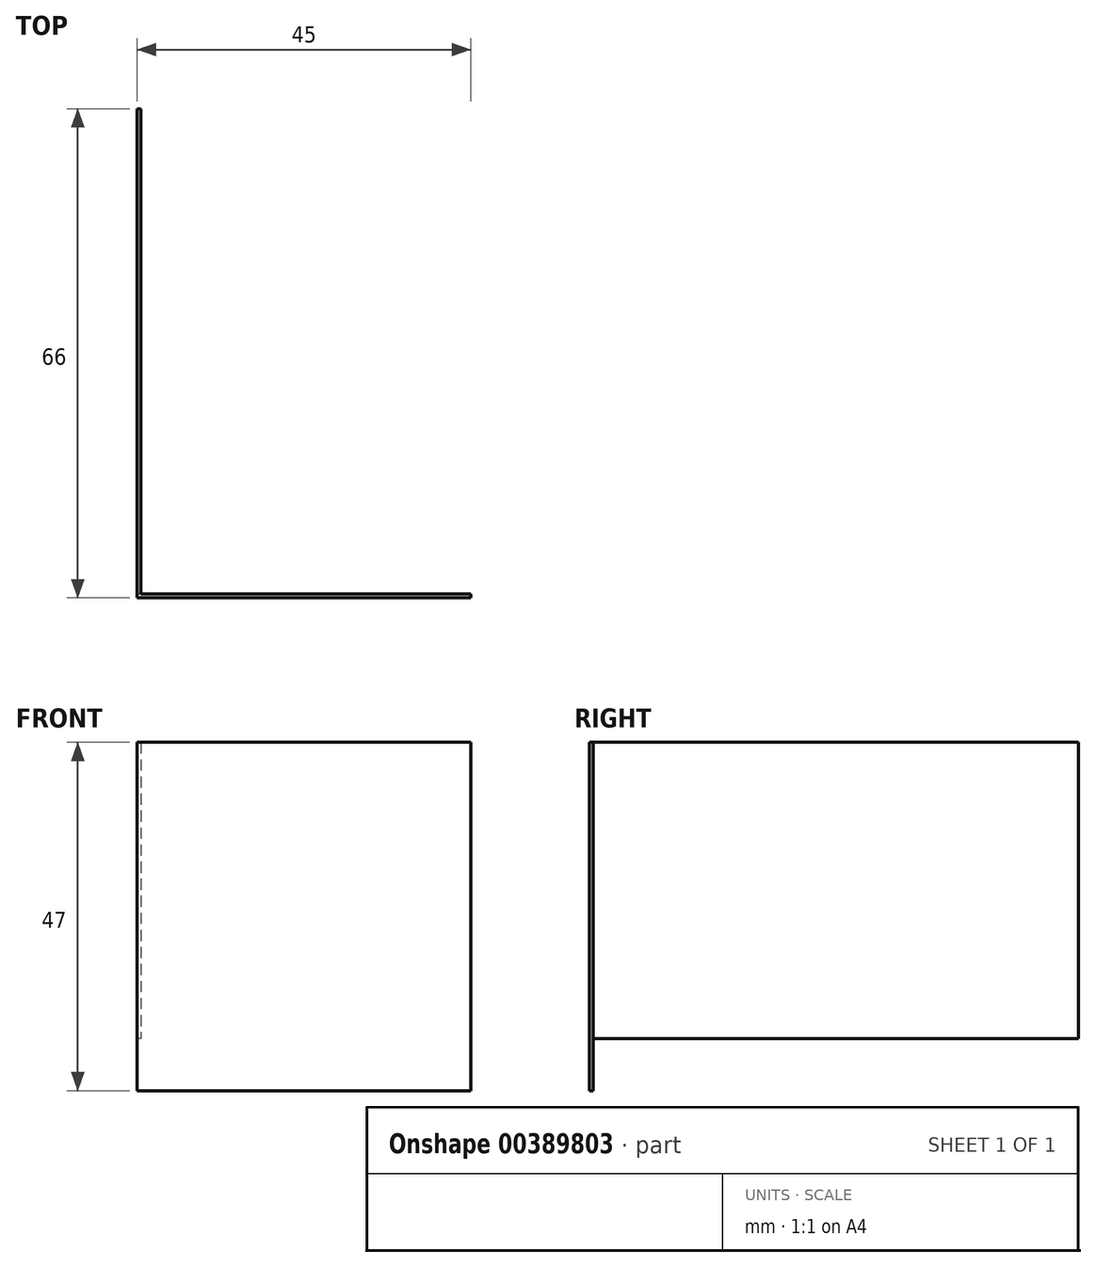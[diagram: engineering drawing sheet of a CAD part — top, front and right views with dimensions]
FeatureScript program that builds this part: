
annotation { "Feature Type Name" : "Feature", "Feature Type Description" : "" }
export const myFeature = defineFeature(function(context is Context, id is Id, definition is map)
    precondition{}
    {
        {
            var Q0;
            Q0=qCreatedBy(makeId("Front.planeOp"),FACE);
            var sketch = newSketch(context, id + "F0", { "sketchPlane" : qUnion([Q0])});
            skLineSegment(sketch, "E0.bottom", {"start": v(0, 0) * mm, "end": v(45, 0) * mm});
            skLineSegment(sketch, "E0.top", {"start": v(0, -47) * mm, "end": v(45, -47) * mm});
            skLineSegment(sketch, "E0.left", {"start": v(0, 0) * mm, "end": v(0, -47) * mm});
            skLineSegment(sketch, "E0.right", {"start": v(45, 0) * mm, "end": v(45, -47) * mm});
            skSolve(sketch);
        }
        {
            var Q0;
            Q0=qSketchRegion(id+"F0",true);
            extrude(context, id + "F1", {"entities" : qUnion([Q0]), "depth" : 0.5 * mm});
        }
        {
            var Q0;
            Q0=qCreatedBy(makeId("Right.planeOp"),FACE);
            var sketch = newSketch(context, id + "F2", { "sketchPlane" : qUnion([Q0])});
            skLineSegment(sketch, "E1.bottom", {"start": v(0, 0) * mm, "end": v(65.5, 0) * mm});
            skLineSegment(sketch, "E1.top", {"start": v(0, -40) * mm, "end": v(65.5, -40) * mm});
            skLineSegment(sketch, "E1.left", {"start": v(0, 0) * mm, "end": v(0, -40) * mm});
            skLineSegment(sketch, "E1.right", {"start": v(65.5, 0) * mm, "end": v(65.5, -40) * mm});
            skSolve(sketch);
        }
        {
            var Q0;
            Q0=qSketchRegion(id+"F2",true);
            extrude(context, id + "F3", {"entities" : qUnion([Q0]), "operationType" : NewBodyOperationType.ADD, "depth" : 0.5 * mm});
        }
    });
